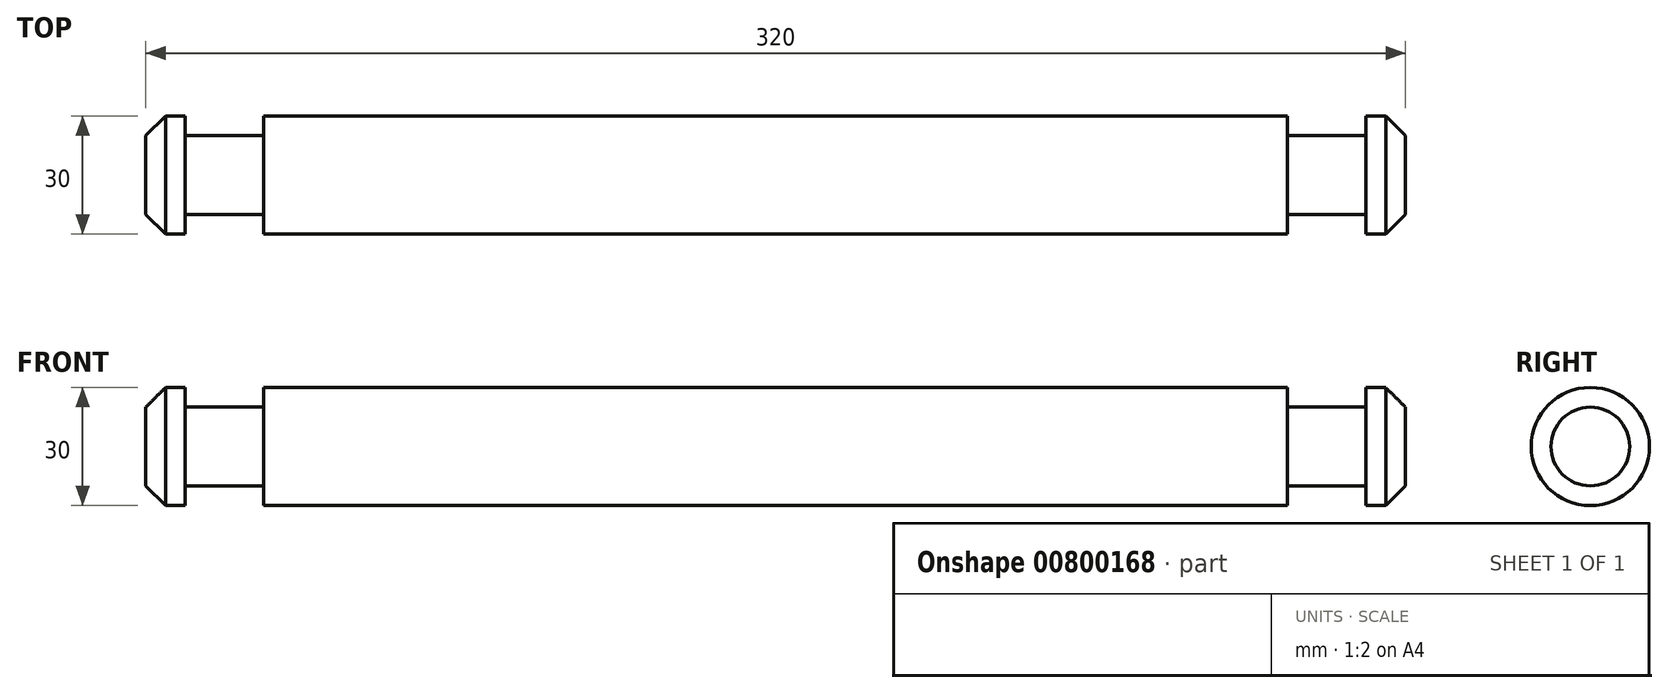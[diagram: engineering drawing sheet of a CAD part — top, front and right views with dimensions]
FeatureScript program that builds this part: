
annotation { "Feature Type Name" : "Feature", "Feature Type Description" : "" }
export const myFeature = defineFeature(function(context is Context, id is Id, definition is map)
    precondition{}
    {
        {
            var Q0;
            Q0=qCreatedBy(makeId("Front.planeOp"),FACE);
            var sketch = newSketch(context, id + "F0", { "sketchPlane" : qUnion([Q0])});
            skLineSegment(sketch, "E0", {"start": v(50, 0) * mm, "end": v(210, 0) * mm});
            skLineSegment(sketch, "E1", {"start": v(210, 0) * mm, "end": v(210, 10) * mm});
            skLineSegment(sketch, "E2", {"start": v(210, 10) * mm, "end": v(205, 15) * mm});
            skLineSegment(sketch, "E3", {"start": v(205, 15) * mm, "end": v(200, 15) * mm});
            skLineSegment(sketch, "E4", {"start": v(200, 15) * mm, "end": v(200, 10) * mm});
            skLineSegment(sketch, "E5", {"start": v(200, 10) * mm, "end": v(180, 10) * mm});
            skLineSegment(sketch, "E6", {"start": v(180, 10) * mm, "end": v(180, 15) * mm});
            skLineSegment(sketch, "E7", {"start": v(180, 15) * mm, "end": v(-80, 15) * mm});
            skLineSegment(sketch, "E8", {"start": v(-80, 15) * mm, "end": v(-80, 10) * mm});
            skLineSegment(sketch, "E9", {"start": v(-80, 10) * mm, "end": v(-100, 10) * mm});
            skLineSegment(sketch, "E10", {"start": v(-100, 10) * mm, "end": v(-100, 15) * mm});
            skLineSegment(sketch, "E11", {"start": v(-100, 15) * mm, "end": v(-105, 15) * mm});
            skLineSegment(sketch, "E12", {"start": v(-105, 15) * mm, "end": v(-110, 10) * mm});
            skLineSegment(sketch, "E13", {"start": v(-110, 10) * mm, "end": v(-110, 0) * mm});
            skLineSegment(sketch, "E14", {"start": v(-110, 0) * mm, "end": v(50, 0) * mm});
            skSolve(sketch);
        }
        {
            var Q0;
            Q0=makeQuery(id+"F0.imprint","IMPRINT",FACE,{"disambiguationData":[TD([[makeQuery(id+"F0.imprint","IMPRINT",EDGE,{"derivedFrom":sQuery(id+"F0.wireOp",EDGE,"E0")}),1.0]])]});
            var Q1;
            Q1=sQuery(id+"F0.wireOp",EDGE,"E14");
            revolve(context, id + "F1", {"surfaceOperationType" : NewSurfaceOperationType.NEW, "entities" : qUnion([Q0]), "axis" : qUnion([Q1]), "revolveType" : RevolveType.FULL});
        }
    });
